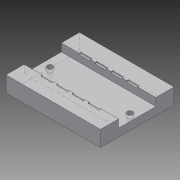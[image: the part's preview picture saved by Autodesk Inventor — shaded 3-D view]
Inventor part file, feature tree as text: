
AUTODESK INVENTOR PART (.ipt)
format: ipt  version: 2013 (Build 170138000, 138)  size: 169,984 bytes
history: native  units: mm
features: sketch x4, extrude x3, fillet x2, hole x1, projected_geometry x1
ambient origin geometry x8: Origin, YZ Plane, XZ Plane, XY Plane, X Axis, Y Axis, Z Axis, Center Point
bodies: Volumenkörper1 (feature_tree)
feature tree (11):
  extrude  "Extrusion1"  Depth=140.0mm
  extrude  "Extrusion2"  Depth=71.0mm
  extrude  "Extrusion3"  Depth=34.5mm
  fillet  "Rundung1"  Radius=180.0mm
  fillet  "Rundung2"  Radius=21.0mm
  hole  "Bohrung1"  [1 undecoded]
  sketch  "Skizze1"  dims[d0=180.0mm d1=140.0mm]
  sketch  "Skizze3"  dims[d2=30.0mm d3=0.0mm d6=71.0mm]
  sketch  "Skizze4"  dims[d7=15.0mm d8=34.5mm d9=180.0mm d10=0.0mm d11=21.0mm]
  projected_geometry  "Projizierte Kontur1"
  sketch  "Skizze5"  dims[d12=77.0mm d13=3.0mm d14=34.5mm d15=40.0mm d17=30.0mm d18=10.0mm d20=10.0mm d22=2.0mm d23=0.0mm d24=1.0mm d25=1.0mm d26=152.4mm d28=13.8mm d29=6.756mm d30=6.0mm d31=11.113mm d32=6.35mm d33=90.0deg d34=20.0mm d35=20.594885mm]
note: 1 required parameter value undecoded (feature->parameter linkage not recoverable at this tier; creation-order binding heuristic only, values carry confidence <= 0.55)
